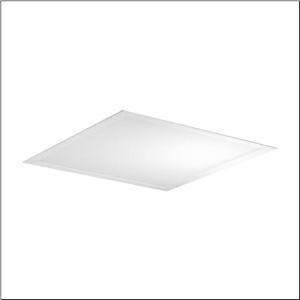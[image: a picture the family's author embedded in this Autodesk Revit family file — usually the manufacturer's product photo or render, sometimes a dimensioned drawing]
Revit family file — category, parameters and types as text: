
# Revit family: apollon_r__21_square_51mq11wd2114_d47a
name_source: partatom
category: Lighting Fixtures
units: mm (PartAtom-declared; Revit-internal decimal feet)

## family parameters
Cut with Voids When Loaded = No
Host = Face
Light Source = No
Part Type = Normal
Room Calculation Point = No
Round Connector Dimension = Use Diameter
Shared = No

## types (1)
- Apollon® 21 square (1 x LED, 4100 lm, 24.7 W, 4000K)
    Apparent Load = 25 VA
    CIE Flux Codes = 60 87 97 100 100
    Color Rendering = 90
    Color Temperature = 4000K
    Default Elevation = 1800 mm
    Description = Apollon® 21 square, office luminaire, primary optical cover: micro prismatic cover, of PMMA, CAT 2 (L<= 3000cd/m²), light emission: direct distribution, primary light characteristic: symmetric, installation type: lay-in mounting, LED, rated luminous flux: 4.100lm, luminous efficacy: 166lm/W, light colour: 940, colour temperature: 4000K, with terminal, 5-pole, mains connection: 220..240V, AC/DC, 0/50..60Hz, rated input power: 24.7W, housing, of aluminium, coated, traffic white (RAL 9016), module: M625, length: 620mm, width: 620mm, height: 30mm, housing upper side, of sheet steel, galvanised, protection rating (complete): IP20, protection rating (lamp compartment, on room side): IP50, insulation class (complete): insulation class II (safety insulation), certification: CE, ENEC, impact resistance: IK03, permissible operating ambient temperature: -20..+45°C, permissible storage temperature: -40..+80°C, packaging unit: 1 piece
    Height = 0 mm  [stored 0 ft]
    Lamp = 1 x LED
    Lamp Light Flux = 4100 lm
    Lamp Power = 24.7 W
    Lamp count = 1
    Length = 620 mm
    Luminous efficacy = 166 lm/W
    Manufacturer = Siteco
    ModVariant = No
    Model = 51MQ11WD2114
    Mounting Place = Ceiling
    Mounting Type = Recessed
    Number of Poles = 1
    OnlyDefault = Yes
    Power Factor = 1
    Product Name = Apollon® 21 square
    Product group = office luminaire | ceiling recessed
    ProductGroupID = 401
    Protection Class = Protection class II
    Protection Degree = IP 20
    RLX_Detail_Level = 1
    RLX_Emergency_Light_Flux = 0 lm
    RLX_Emergency_Type = 0
    RLX_Emergency_Type_DB = No
    RlxData = <blob elided: 12949 chars, md5=d884350f>
    Socket = socket
    Standby Power = 0 W
    System Light Flux = 4100 lm
    System Power = 25 W
    Type Comments = Product without accessories
    Type Image = l_1291054.jpg
    URL = http://relux.com
    VarID = ---
    Voltage = 0 V
    Weight = 0.00 kg
    Width = 620 mm

note: [stored X ft] marks values corroborated as IEEE doubles in the binary element streams (Revit-internal decimal feet)

## geometry (parser evidence)
native form markers: Sweep x9
no freeform markers — native parametric forms only
